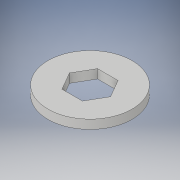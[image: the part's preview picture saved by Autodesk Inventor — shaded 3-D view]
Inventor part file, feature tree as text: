
AUTODESK INVENTOR PART (.ipt)
format: ipt  version: 2019 (Build 230136000, 136)  size: 103,424 bytes
history: native  units: mm
features: other x1, extrude x1, sketch x1
ambient origin geometry x8: Origin, YZ Plane, XZ Plane, XY Plane, X Axis, Y Axis, Z Axis, Center Point
bodies: Body1 (feature_tree)
feature tree (3):
  other  "Sólido1"
  extrude  "Extrusión1"  TaperAngle=0.0deg  [1 undecoded]
  sketch  "Boceto1"  dims[d0=12.7mm d1=0.0mm d2=30.0mm d3=3.18mm d4=0.0mm]
note: 1 required parameter value undecoded (feature->parameter linkage not recoverable at this tier; creation-order binding heuristic only, values carry confidence <= 0.55)
